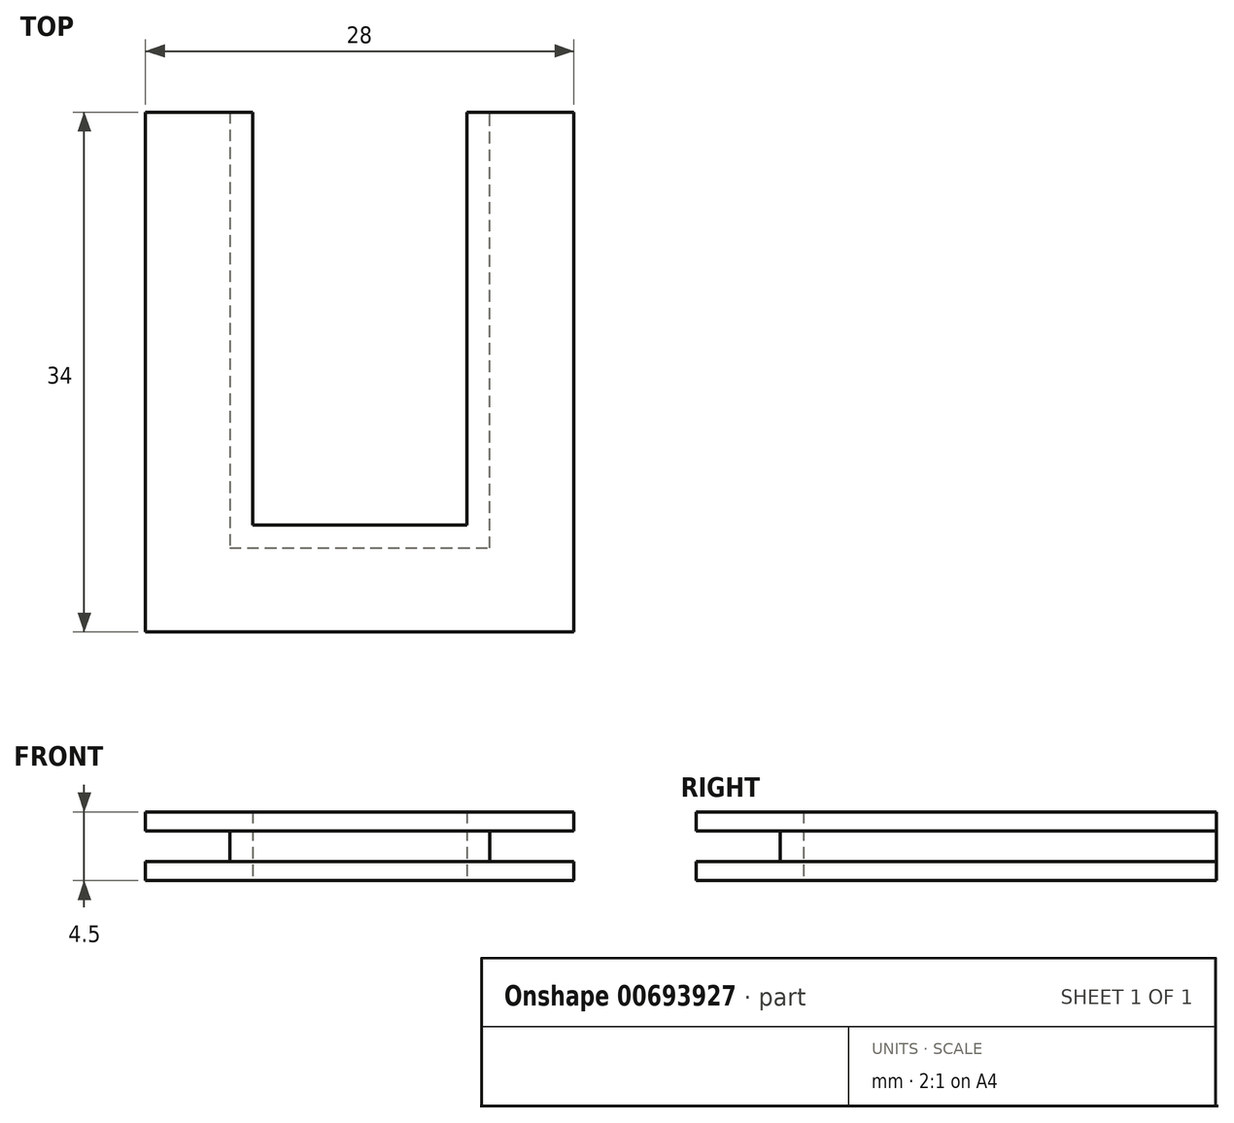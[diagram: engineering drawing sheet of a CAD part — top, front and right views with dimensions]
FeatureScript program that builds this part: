
annotation { "Feature Type Name" : "Feature", "Feature Type Description" : "" }
export const myFeature = defineFeature(function(context is Context, id is Id, definition is map)
    precondition{}
    {
        {
            var Q0;
            Q0=qCreatedBy(makeId("Top.planeOp"),FACE);
            var sketch = newSketch(context, id + "F0", { "sketchPlane" : qUnion([Q0])});
            skLineSegment(sketch, "E0.top", {"start": v(14, -17) * mm, "end": v(-14, -17) * mm});
            skLineSegment(sketch, "E0.left", {"start": v(14, 17) * mm, "end": v(14, -17) * mm});
            skLineSegment(sketch, "E0.right", {"start": v(-14, 17) * mm, "end": v(-14, -17) * mm});
            skPoint(sketch, "E0.middle", {"position": v(0, 0) * mm});
            skLineSegment(sketch, "E1.top", {"start": v(-7, -10) * mm, "end": v(7, -10) * mm});
            skLineSegment(sketch, "E1.left", {"start": v(-7, 17) * mm, "end": v(-7, -10) * mm});
            skLineSegment(sketch, "E1.right", {"start": v(7, 17) * mm, "end": v(7, -10) * mm});
            skLineSegment(sketch, "E2", {"start": v(-14, 17) * mm, "end": v(-7, 17) * mm});
            skLineSegment(sketch, "E3", {"start": v(7, 17) * mm, "end": v(14, 17) * mm});
            skSolve(sketch);
        }
        {
            var Q0;
            Q0 = qSketchRegion(id + "F0", true);
            extrude(context, id + "F1", {"entities" : qUnion([Q0]), "depth" : 4.5 * mm, "offsetDistance" : 25 * mm});
        }
        {
            var Q0;
            Q0=makeQuery(id+"F1.opExtrude","SWEPT_FACE",FACE,{"disambiguationData":[OSD([sQuery(id+"F0.wireOp",EDGE,"E0.right")])]});
            var sketch = newSketch(context, id + "F2", { "sketchPlane" : qUnion([Q0])});
            skLineSegment(sketch, "E4", {"start": v(-17, 3.25) * mm, "end": v(17, 3.25) * mm});
            skLineSegment(sketch, "E5", {"start": v(-17, 1.25) * mm, "end": v(17, 1.25) * mm});
            skLineSegment(sketch, "E6", {"start": v(-17, 3.25) * mm, "end": v(-17, 4.5) * mm});
            skLineSegment(sketch, "E7", {"start": v(-17, 1.25) * mm, "end": v(-17, 0) * mm});
            skSolve(sketch);
        }
        {
            var Q0;
            {var subQ0=sQuery(id+"F2.wireOp",EDGE,"E4");Q0=makeQuery(id+"F2.imprint","IMPRINT",FACE,{"disambiguationData":[TD([[makeQuery(id+"F2.imprint","IMPRINT",EDGE,{"derivedFrom":subQ0}),-1.0]])]});}
            extrude(context, id + "F3", {"entities" : qUnion([Q0]), "operationType" : NewBodyOperationType.REMOVE, "oppositeDirection" : true, "depth" : 5.5 * mm, "offsetDistance" : 25 * mm});
        }
        {
            var Q0;
            Q0=makeQuery(id+"F1.opExtrude","SWEPT_FACE",FACE,{"disambiguationData":[OSD([sQuery(id+"F0.wireOp",EDGE,"E0.left")])]});
            var sketch = newSketch(context, id + "F4", { "sketchPlane" : qUnion([Q0])});
            skLineSegment(sketch, "E8", {"start": v(-17, 3.25) * mm, "end": v(17, 3.25) * mm});
            skLineSegment(sketch, "E9", {"start": v(-17, 1.25) * mm, "end": v(17, 1.25) * mm});
            skLineSegment(sketch, "E10", {"start": v(-17, 3.25) * mm, "end": v(-17, 4.5) * mm});
            skLineSegment(sketch, "E11", {"start": v(-17, 0) * mm, "end": v(-17, 1.25) * mm});
            skSolve(sketch);
        }
        {
            var Q0;
            {var subQ0=sQuery(id+"F4.wireOp",EDGE,"E8");Q0=makeQuery(id+"F4.imprint","IMPRINT",FACE,{"disambiguationData":[TD([[makeQuery(id+"F4.imprint","IMPRINT",EDGE,{"derivedFrom":subQ0}),-1.0]])]});}
            extrude(context, id + "F5", {"entities" : qUnion([Q0]), "operationType" : NewBodyOperationType.REMOVE, "oppositeDirection" : true, "depth" : 5.5 * mm, "offsetDistance" : 25 * mm});
        }
        {
            var Q0;
            Q0=makeQuery(id+"F1.opExtrude","SWEPT_FACE",FACE,{"disambiguationData":[OSD([sQuery(id+"F0.wireOp",EDGE,"E0.top")])]});
            var sketch = newSketch(context, id + "F6", { "sketchPlane" : qUnion([Q0])});
            skLineSegment(sketch, "E12", {"start": v(-8.5, 1.25) * mm, "end": v(8.5, 1.25) * mm});
            skLineSegment(sketch, "E13", {"start": v(-8.5, 3.25) * mm, "end": v(8.5, 3.25) * mm});
            skSolve(sketch);
        }
        {
            var Q0;
            Q0 = qSketchRegion(id + "F6", true);
            var Q1;
            Q1=makeQuery(id+"F6.imprint","IMPRINT",FACE,{"disambiguationData":[TD([[makeQuery(id+"F6.imprint","IMPRINT",EDGE,{"derivedFrom":sQuery(id+"F6.wireOp",EDGE,"E12")}),1.0]])]});
            extrude(context, id + "F7", {"entities" : qUnion([Q0, Q1]), "operationType" : NewBodyOperationType.REMOVE, "oppositeDirection" : true, "depth" : 5.5 * mm, "offsetDistance" : 25 * mm});
        }
    });
